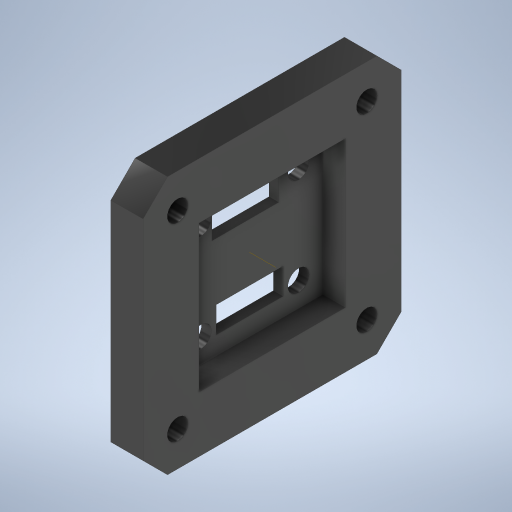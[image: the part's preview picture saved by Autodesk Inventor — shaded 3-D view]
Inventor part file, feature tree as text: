
AUTODESK INVENTOR PART (.ipt)
format: ipt  version: 2023 (Build 270158000, 158)  size: 310,784 bytes
history: native  units: mm
features: sketch x6, extrude x4, hole x2, chamfer x1
ambient origin geometry x8: Origin, YZ Plane, XZ Plane, XY Plane, X Axis, Y Axis, Z Axis, Center Point
bodies: Volumenkörper1 (feature_tree)
feature tree (13):
  extrude  "Extrusion1"  Depth=42.3mm
  extrude  "Extrusion2"  Depth=24.0mm
  hole  "Bohrung1"  [1 undecoded]
  hole  "Bohrung2"  [1 undecoded]
  chamfer  "Fase1"  Distance=8.0mm
  sketch  "Skizze5"  dims[d17=8.0mm]
  sketch  "Skizze6"  dims[d18=8.0mm d19=8.0mm d20=8.0mm d21=8.0mm d22=8.0mm d23=8.0mm d24=3.4mm d25=6.0mm d26=4.0mm d27=2.0mm d28=90.0deg d29=8.0mm d30=20.594885mm d31=15.5mm d32=15.5mm d33=15.5mm d34=15.5mm d35=15.5mm d36=15.5mm d37=15.5mm d38=15.5mm d39=4.0mm d40=2.0mm d41=45.0deg d42=11.0mm d43=4.3mm d44=3.0mm d45=5.8mm d46=11.0mm d47=4.3mm d48=3.0mm d49=5.5mm d50=10.0mm d51=0.0mm d52=10.0mm d53=0.0mm d54=0.5mm d55=0.872665mm d56=0.5mm d57=0.872665mm]
  extrude  "Extrusion3"  Depth=10.0mm
  extrude  "Extrusion4"  Depth=10.0mm
  sketch  "Skizze1"  dims[d0=42.3mm d1=42.3mm]
  sketch  "Skizze2"  dims[d2=5.3mm d3=0.0mm d4=24.0mm]
  sketch  "Skizze3"  dims[d5=24.0mm d6=3.7mm d7=0.0mm]
  sketch  "Skizze4"  dims[d9=3.5mm d10=6.0mm d11=4.0mm d12=2.0mm d13=90.0deg d14=8.0mm d15=20.594885mm d16=8.0mm]
note: 2 required parameter values undecoded (feature->parameter linkage not recoverable at this tier; creation-order binding heuristic only, values carry confidence <= 0.55)
